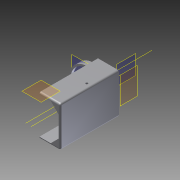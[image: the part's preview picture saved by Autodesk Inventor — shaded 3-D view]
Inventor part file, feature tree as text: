
AUTODESK INVENTOR PART (.ipt)
format: ipt  version: 2012 (Build 160160000, 160)  size: 836,096 bytes
history: native  units: mm
features: sketch x31, extrude x31, reference x30, projected_geometry x23, fillet x12, plane x5, other x3
ambient origin geometry x8: Origin, YZ Plane, XZ Plane, XY Plane, X Axis, Y Axis, Z Axis, Center Point
bodies: Solid1 (feature_tree)
feature tree (135):
  plane  "Work Plane2"
  sketch  "Sketch3"  dims[d1=0.3mm d2=0.3mm]
  plane  "Work Plane3"
  extrude  "Extrusion1"  Depth=0.3mm
  extrude  "Extrusion2"  Depth=10.0mm TaperAngle=0.0deg
  plane  "Work Plane4"
  extrude  "Extrusion3"  Depth=10.0mm TaperAngle=0.0deg
  extrude  "Extrusion4"  Depth=2.0mm
  extrude  "Extrusion5"  Depth=2.0mm
  extrude  "Extrusion6"  Depth=2.0mm TaperAngle=0.0deg
  extrude  "Extrusion7"  TaperAngle=0.0deg  [1 undecoded]
  extrude  "Extrusion8"  TaperAngle=0.0deg  [1 undecoded]
  fillet  "Fillet3"  Radius=20.0mm
  fillet  "Fillet4"  Radius=20.0mm
  fillet  "Fillet5"  Radius=0.3mm
  extrude  "Extrusion10"  Depth=0.3mm
  extrude  "Extrusion11"  Depth=0.3mm TaperAngle=0.0deg
  extrude  "Extrusion12"  Depth=1.0mm
  extrude  "Extrusion13"  Depth=2.0mm TaperAngle=0.0deg
  extrude  "Extrusion14"  Depth=0.3mm
  extrude  "Extrusion15"  Depth=0.3mm
  extrude  "Extrusion16"  TaperAngle=0.0deg  [1 undecoded]
  extrude  "Extrusion17"  Depth=2.0mm
  extrude  "Extrusion18"  Depth=2.0mm TaperAngle=0.0deg
  extrude  "Extrusion20"  Depth=14.0mm
  extrude  "Extrusion21"  Depth=7.0mm TaperAngle=0.0deg
  plane  "Work Plane5"
  extrude  "Extrusion22"  Depth=3.3mm
  extrude  "Extrusion23"  Depth=3.3mm
  extrude  "Extrusion24"  Depth=0.3mm
  extrude  "Extrusion25"  Depth=0.3mm
  plane  "Work Plane7"
  extrude  "Extrusion26"  Depth=20.0mm TaperAngle=0.0deg
  extrude  "Extrusion27"  Depth=0.3mm
  extrude  "Extrusion28"  Depth=0.3mm
  extrude  "Extrusion29"  Depth=2.0mm
  extrude  "Extrusion30"  Depth=2.0mm
  extrude  "Extrusion31"  TaperAngle=45.0deg  [1 undecoded]
  extrude  "Extrusion34"  Depth=9.0mm
  other  "Work Axis2"
  fillet  "Fillet47"  Radius=10.0mm
  fillet  "Fillet48"  [1 undecoded]
  fillet  "Fillet49"  Radius=10.0mm
  fillet  "Fillet50"  Radius=10.0mm
  fillet  "Fillet51"  Radius=10.0mm
  fillet  "Fillet52"  Radius=0.3mm
  fillet  "Fillet53"  Radius=0.3mm
  fillet  "Fillet54"  Radius=10.0mm
  fillet  "Fillet55"  Radius=10.0mm
  other  "Work Axis3"
  extrude  "Extrusion35"  Depth=4.0mm
  other  "Work Axis4"
  reference  "Reference32"
  sketch  "Sketch4"  dims[d3=2.0mm d4=10.0mm d5=0.0mm]
  reference  "Reference33"
  sketch  "Sketch5"  dims[d6=0.3mm d7=10.0mm d8=0.0mm]
  sketch  "Sketch7"  dims[d9=2.0mm d10=2.0mm]
  projected_geometry  "Projected Loop3"
  sketch  "Sketch8"  dims[d11=2.0mm d12=2.0mm]
  sketch  "Sketch10"  dims[d13=120.0mm d14=2.0mm d15=0.0mm]
  reference  "Reference36"
  sketch  "Sketch11"  dims[d24=2.0mm d25=0.0mm]
  reference  "Reference37"
  sketch  "Sketch12"  dims[d26=2.0mm d27=0.0mm d28=20.0mm d29=0.0mm d31=20.0mm d32=0.0mm d34=0.3mm]
  sketch  "Sketch15"  dims[d35=20.0mm d36=0.0mm d37=0.3mm]
  projected_geometry  "Projected Loop5"
  projected_geometry  "Projected Loop6"
  sketch  "Sketch16"  dims[d38=10.0mm d39=0.0mm d40=0.3mm d41=0.0mm]
  reference  "Reference46"
  reference  "Reference47"
  reference  "Reference48"
  reference  "Reference49"
  reference  "Reference50"
  reference  "Reference51"
  reference  "Reference52"
  reference  "Reference53"
  sketch  "Sketch17"  dims[d43=1.0mm d44=1.0mm]
  reference  "Reference54"
  reference  "Reference55"
  reference  "Reference56"
  reference  "Reference57"
  reference  "Reference58"
  reference  "Reference59"
  reference  "Reference60"
  reference  "Reference61"
  sketch  "Sketch18"  dims[d45=1.0mm d52=2.0mm d53=0.0mm]
  reference  "Reference62"
  sketch  "Sketch19"  dims[d58=2.0mm d59=0.0mm d60=0.3mm]
  projected_geometry  "Projected Loop7"
  projected_geometry  "Projected Loop8"
  sketch  "Sketch20"  dims[d61=0.3mm d62=0.3mm]
  projected_geometry  "Projected Loop9"
  projected_geometry  "Projected Loop10"
  sketch  "Sketch21"  dims[d63=0.3mm d64=0.0mm]
  projected_geometry  "Projected Loop11"
  sketch  "Sketch22"  dims[d66=0.0mm d67=2.0mm]
  reference  "Reference63"
  reference  "Reference64"
  reference  "Reference65"
  reference  "Reference66"
  reference  "Reference67"
  reference  "Reference68"
  reference  "Reference69"
  reference  "Reference70"
  sketch  "Sketch23"  dims[d68=2.0mm d69=2.0mm d70=0.0mm]
  projected_geometry  "Projected Loop12"
  projected_geometry  "Projected Loop13"
  projected_geometry  "Projected Loop14"
  projected_geometry  "Projected Loop15"
  sketch  "Sketch25"  dims[d72=2.0mm d73=0.0mm d74=14.0mm]
  projected_geometry  "Projected Loop16"
  sketch  "Sketch26"  dims[d78=2.0mm d79=0.0mm d80=7.0mm d81=0.0mm]
  sketch  "Sketch28"  dims[d82=10.0mm d83=0.0mm d84=3.3mm]
  projected_geometry  "Projected Loop21"
  sketch  "Sketch29"  dims[d85=3.3mm d86=3.3mm]
  projected_geometry  "Projected Loop22"
  projected_geometry  "Projected Loop23"
  sketch  "Sketch30"  dims[d87=3.3mm d88=0.3mm]
  projected_geometry  "Projected Loop24"
  sketch  "Sketch31"  dims[d89=0.3mm d90=0.3mm]
  projected_geometry  "Projected Loop25"
  sketch  "Sketch32"  dims[d91=0.3mm d94=20.0mm d95=0.0mm]
  sketch  "Sketch33"  dims[d97=0.3mm d98=0.3mm]
  projected_geometry  "Projected Loop26"
  sketch  "Sketch34"  dims[d99=0.3mm d100=0.3mm]
  projected_geometry  "Projected Loop27"
  sketch  "Sketch35"  dims[d101=0.3mm d102=0.0mm d103=2.0mm]
  projected_geometry  "Projected Loop28"
  projected_geometry  "Projected Loop29"
  sketch  "Sketch37"  dims[d104=2.0mm d105=2.0mm]
  sketch  "Sketch38"  dims[d106=2.0mm d111=45.0deg]
  projected_geometry  "Projected Loop31"
  sketch  "Sketch41"  dims[d112=9.0mm d113=9.0mm d114=10.0mm d115=0.0mm d116=0.0mm d117=0.0mm d123=10.0mm d124=0.0mm d132=10.0mm d133=0.0mm d134=10.0mm d135=0.0mm d138=0.3mm d139=0.0mm d151=0.3mm d152=0.0mm d153=10.0mm d154=0.0mm d155=10.0mm d156=0.0mm]
  reference  "Reference73"
  sketch  "Sketch42"  dims[d157=10.0mm d158=0.0mm d159=4.0mm d160=10.0mm d161=0.0mm d162=10.0mm d163=0.0mm d186=25.4mm d187=0.0mm d189=1.0mm d190=2.0mm d191=2.0mm d192=2.0mm d193=2.0mm d194=1.0mm d195=2.0mm d196=2.0mm d197=1.5mm d198=78.5mm d199=0.0mm]
note: 5 required parameter values undecoded (feature->parameter linkage not recoverable at this tier; creation-order binding heuristic only, values carry confidence <= 0.55)
